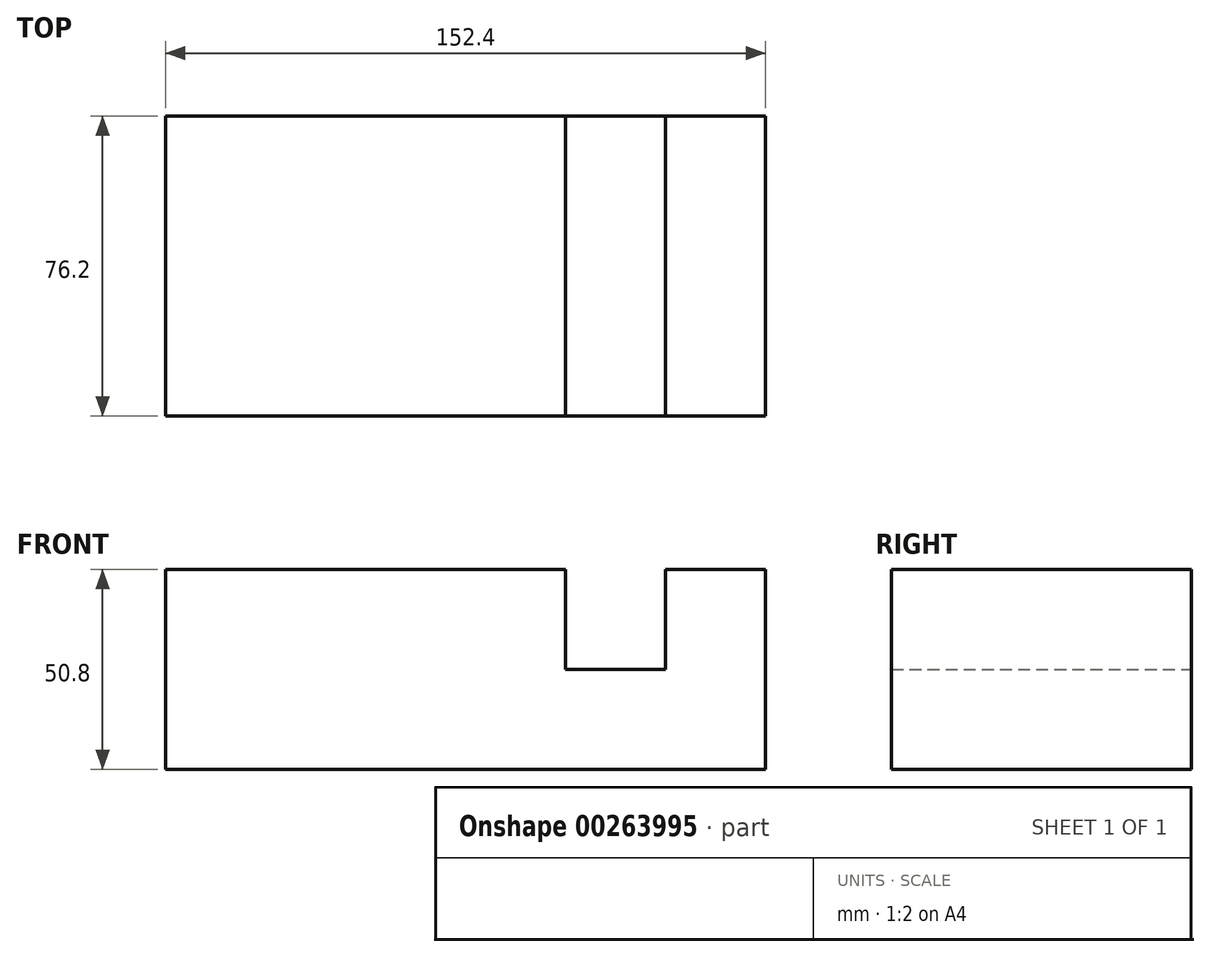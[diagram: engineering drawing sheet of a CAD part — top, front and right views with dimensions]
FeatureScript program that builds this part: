
annotation { "Feature Type Name" : "Feature", "Feature Type Description" : "" }
export const myFeature = defineFeature(function(context is Context, id is Id, definition is map)
    precondition{}
    {
        {
            var Q0;
            Q0=qCreatedBy(makeId("Front.planeOp"),FACE);
            var sketch = newSketch(context, id + "F0", { "sketchPlane" : qUnion([Q0])});
            skLineSegment(sketch, "E0", {"start": v(-77.2, -39.68) * mm, "end": v(75.2, -39.68) * mm});
            skLineSegment(sketch, "E1", {"start": v(-77.2, -39.68) * mm, "end": v(-77.2, 11.12) * mm});
            skLineSegment(sketch, "E2", {"start": v(-77.2, 11.12) * mm, "end": v(24.4, 11.12) * mm});
            skLineSegment(sketch, "E3", {"start": v(24.4, 11.12) * mm, "end": v(24.4, -14.28) * mm});
            skLineSegment(sketch, "E4", {"start": v(24.4, -14.28) * mm, "end": v(49.8, -14.28) * mm});
            skLineSegment(sketch, "E5", {"start": v(49.8, 11.12) * mm, "end": v(49.8, -14.28) * mm});
            skLineSegment(sketch, "E6", {"start": v(49.8, 11.12) * mm, "end": v(75.2, 11.12) * mm});
            skLineSegment(sketch, "E7", {"start": v(75.2, 11.12) * mm, "end": v(75.2, -39.68) * mm});
            skSolve(sketch);
        }
        {
            var Q0;
            Q0 = qSketchRegion(id + "F0", true);
            extrude(context, id + "F1", {"entities" : qUnion([Q0]), "depth" : 76.2 * mm});
        }
    });
